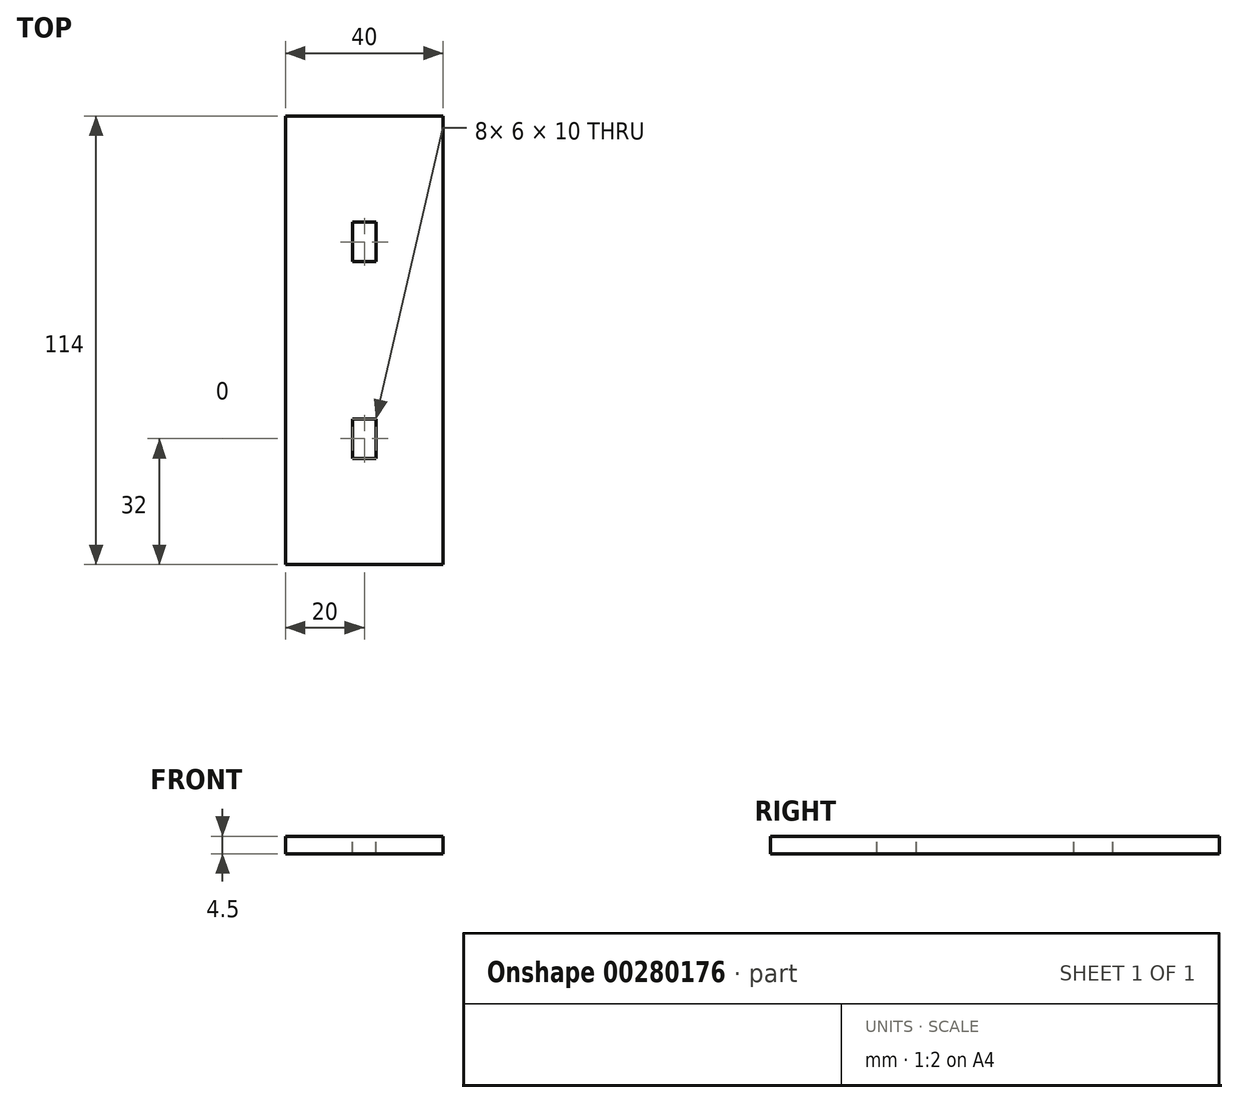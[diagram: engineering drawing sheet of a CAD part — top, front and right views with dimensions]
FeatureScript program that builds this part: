
annotation { "Feature Type Name" : "Feature", "Feature Type Description" : "" }
export const myFeature = defineFeature(function(context is Context, id is Id, definition is map)
    precondition{}
    {
        {
            var Q0;
            Q0=qCreatedBy(makeId("Top.planeOp"),FACE);
            var sketch = newSketch(context, id + "F0", { "sketchPlane" : qUnion([Q0])});
            skLineSegment(sketch, "E0.bottom", {"start": v(20, -57) * mm, "end": v(-20, -57) * mm});
            skLineSegment(sketch, "E0.top", {"start": v(20, 57) * mm, "end": v(-20, 57) * mm});
            skLineSegment(sketch, "E0.left", {"start": v(20, -57) * mm, "end": v(20, 57) * mm});
            skLineSegment(sketch, "E0.right", {"start": v(-20, -57) * mm, "end": v(-20, 57) * mm});
            skPoint(sketch, "E0.middle", {"position": v(0, 0) * mm});
            skSolve(sketch);
        }
        {
            var Q0;
            Q0 = qSketchRegion(id + "F0", true);
            extrude(context, id + "F1", {"entities" : qUnion([Q0]), "depth" : 4.5 * mm});
        }
        {
            var Q0;
            Q0=makeQuery(id+"F1.opExtrude","CAP_FACE",FACE,{"disambiguationData":[OSD([sQuery(id+"F0.wireOp",EDGE,"E0.bottom"),sQuery(id+"F0.wireOp",EDGE,"E0.top"),sQuery(id+"F0.wireOp",EDGE,"E0.left"),sQuery(id+"F0.wireOp",EDGE,"E0.right")])],"isStart":false});
            var sketch = newSketch(context, id + "F2", { "sketchPlane" : qUnion([Q0])});
            skLineSegment(sketch, "E1.bottom", {"start": v(3, 20) * mm, "end": v(-3, 20) * mm});
            skLineSegment(sketch, "E1.top", {"start": v(3, 30) * mm, "end": v(-3, 30) * mm});
            skLineSegment(sketch, "E1.left", {"start": v(3, 20) * mm, "end": v(3, 30) * mm});
            skLineSegment(sketch, "E1.right", {"start": v(-3, 20) * mm, "end": v(-3, 30) * mm});
            skPoint(sketch, "E1.middle", {"position": v(0, 25) * mm});
            skLineSegment(sketch, "E2.bottom", {"start": v(3, -30) * mm, "end": v(-3, -30) * mm});
            skLineSegment(sketch, "E2.top", {"start": v(3, -20) * mm, "end": v(-3, -20) * mm});
            skLineSegment(sketch, "E2.left", {"start": v(3, -30) * mm, "end": v(3, -20) * mm});
            skLineSegment(sketch, "E2.right", {"start": v(-3, -30) * mm, "end": v(-3, -20) * mm});
            skPoint(sketch, "E2.middle", {"position": v(0, -25) * mm});
            skLineSegment(sketch, "E3", {"start": v(0, 25) * mm, "end": v(0, 0) * mm, "construction": true});
            skLineSegment(sketch, "E4", {"start": v(0, 0) * mm, "end": v(0, -25) * mm, "construction": true});
            skSolve(sketch);
        }
        {
            var Q0;
            Q0 = qSketchRegion(id + "F2", true);
            extrude(context, id + "F3", {"entities" : qUnion([Q0]), "operationType" : NewBodyOperationType.REMOVE, "endBound" : BoundingType.UP_TO_NEXT, "oppositeDirection" : true, "depth" : 25 * mm});
        }
    });
